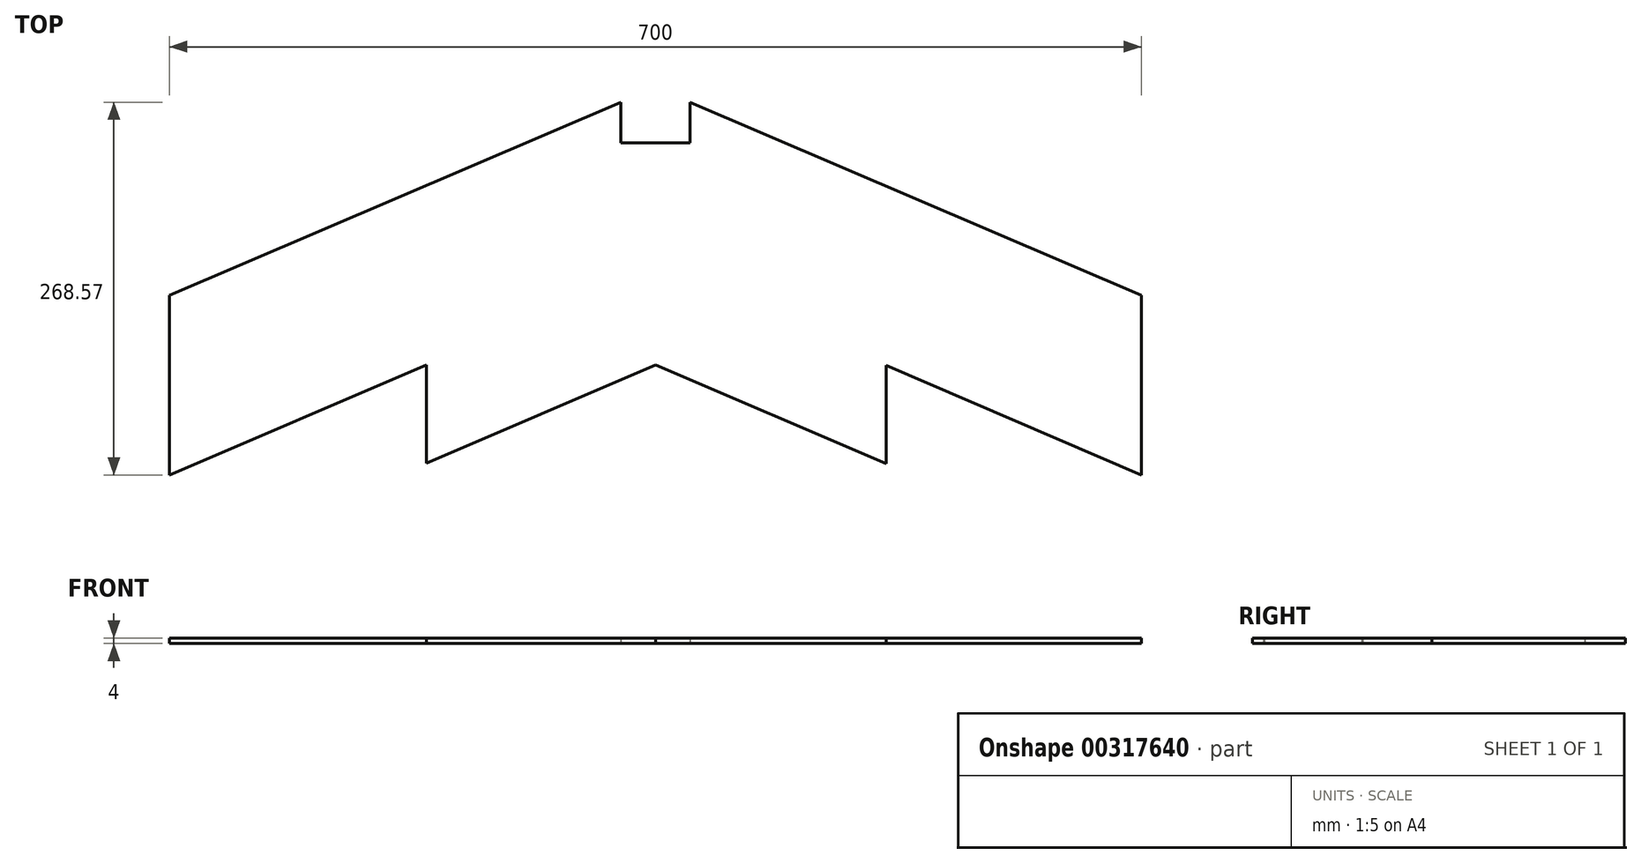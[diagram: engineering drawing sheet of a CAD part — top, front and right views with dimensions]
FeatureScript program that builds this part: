
annotation { "Feature Type Name" : "Feature", "Feature Type Description" : "" }
export const myFeature = defineFeature(function(context is Context, id is Id, definition is map)
    precondition{}
    {
        {
            var Q0;
            Q0=qCreatedBy(makeId("Top.planeOp"),FACE);
            var sketch = newSketch(context, id + "F0", { "sketchPlane" : qUnion([Q0])});
            skLineSegment(sketch, "E0", {"start": v(-25, 189.29) * mm, "end": v(-350, 50) * mm});
            skLineSegment(sketch, "E1", {"start": v(-350, 50) * mm, "end": v(-350, -150) * mm});
            skLineSegment(sketch, "E2", {"start": v(-350, -150) * mm, "end": v(0, 0) * mm});
            skLineSegment(sketch, "E3", {"start": v(25, 189.29) * mm, "end": v(350, 50) * mm});
            skLineSegment(sketch, "E4", {"start": v(350, 50) * mm, "end": v(350, -150) * mm});
            skLineSegment(sketch, "E5", {"start": v(350, -150) * mm, "end": v(0, 0) * mm});
            skLineSegment(sketch, "E6", {"start": v(-350, -79.28) * mm, "end": v(-165, 0) * mm});
            skLineSegment(sketch, "E7", {"start": v(-165, 0) * mm, "end": v(-165, -70.72) * mm});
            skLineSegment(sketch, "E8", {"start": v(350, -79.28) * mm, "end": v(166.17, -0.5) * mm});
            skLineSegment(sketch, "E9", {"start": v(166.17, -0.5) * mm, "end": v(166.17, -71.22) * mm});
            skLineSegment(sketch, "E10", {"start": v(-25, 189.29) * mm, "end": v(-25, 160) * mm});
            skLineSegment(sketch, "E11", {"start": v(-25, 160) * mm, "end": v(25, 160) * mm});
            skLineSegment(sketch, "E12", {"start": v(25, 160) * mm, "end": v(25, 189.29) * mm});
            skPoint(sketch, "E13.end.orphan", {"position": v(0, 200) * mm});
            skSolve(sketch);
        }
        {
            var Q0;
            {var subQ9=sQuery(id+"F0.wireOp",EDGE,"E0");Q0=makeQuery(id+"F0.imprint","IMPRINT",FACE,{"disambiguationData":[TD([[makeQuery(id+"F0.imprint","IMPRINT",EDGE,{"derivedFrom":subQ9}),1.0]])]});}
            extrude(context, id + "F1", {"entities" : qUnion([Q0]), "depth" : 4 * mm});
        }
    });
